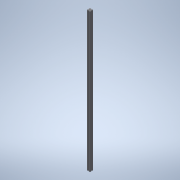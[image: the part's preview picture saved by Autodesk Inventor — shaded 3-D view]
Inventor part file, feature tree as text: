
AUTODESK INVENTOR PART (.ipt)
format: ipt  version: 2022 (Build 260153000, 153)  size: 225,792 bytes
history: native  units: mm (DEFAULTED — no unit token found)
features: other x21, sketch x2, extrude x1, hole x1
ambient origin geometry x8: Origin, YZ Plane, XZ Plane, XY Plane, X Axis, Y Axis, Z Axis, Center Point
bodies: Solid1 (feature_tree)
feature tree (25):
  extrude  "Extrusion1"  TaperAngle=0.0deg  [1 undecoded]
  hole  "Hole1"  [1 undecoded]
  other  "C1_XY"
  other  "C1_YZ"
  other  "C1_ZX"
  other  "C1_X"
  other  "C1_Y"
  other  "C1_Z"
  other  "C1_Center"
  other  "to_frame_cap1_XY"
  other  "to_frame_cap1_YZ"
  other  "to_frame_cap1_ZX"
  other  "to_frame_cap1_X"
  other  "to_frame_cap1_Y"
  other  "to_frame_cap1_Z"
  other  "to_frame_cap1_Center"
  other  "to_frame_cap2_XY"
  other  "to_frame_cap2_YZ"
  other  "to_frame_cap2_ZX"
  other  "to_frame_cap2_X"
  other  "to_frame_cap2_Y"
  other  "to_frame_cap2_Z"
  other  "to_frame_cap2_Center"
  sketch  "Sketch_60"  dims[d2=10.5mm d3=6.0mm d4=4.0mm d5=2.0mm d6=90.0deg d7=1000.0mm d8=0.0mm d9=0.0mm d10=0.0mm d11=0.0mm d12=152.4mm d13=0.872665mm d14=152.4mm d15=0.872665mm]
  sketch  "Sketch2"  dims[d0=2590.8mm d1=0.0mm]
note: 2 required parameter values undecoded (feature->parameter linkage not recoverable at this tier; creation-order binding heuristic only, values carry confidence <= 0.55)
